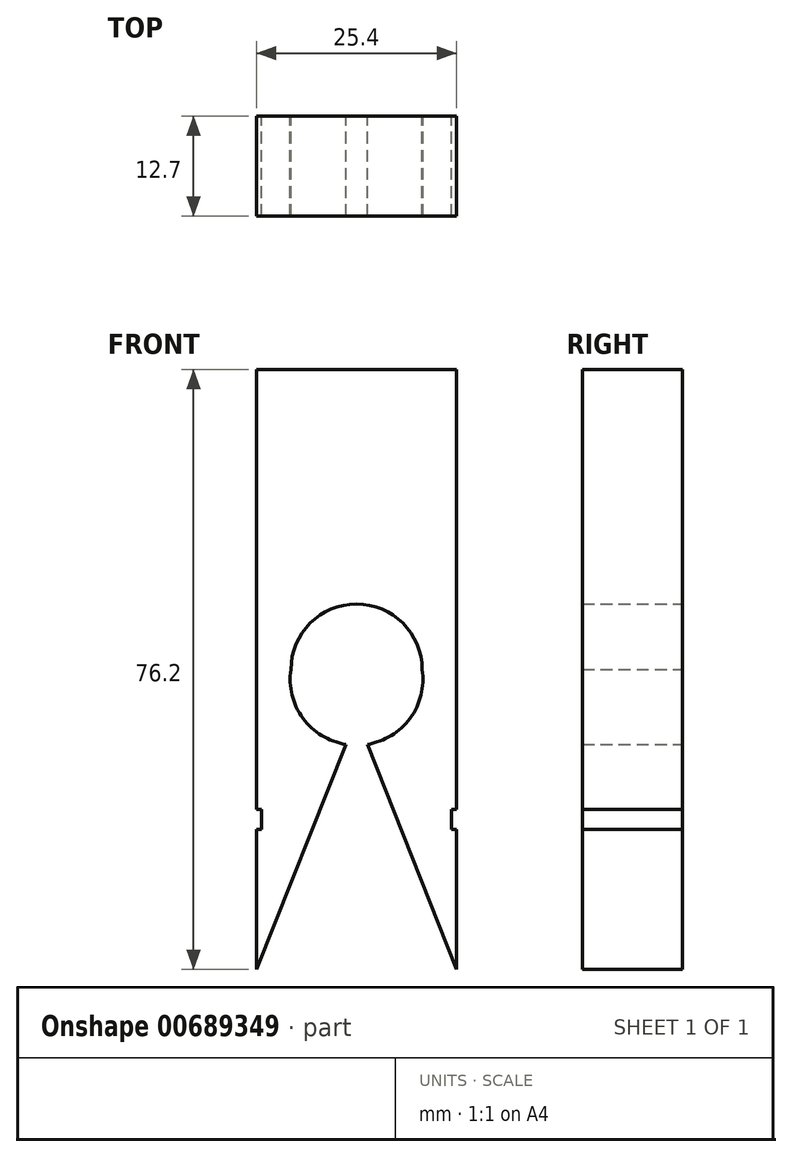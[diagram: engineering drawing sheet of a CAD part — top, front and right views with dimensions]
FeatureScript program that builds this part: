
annotation { "Feature Type Name" : "Feature", "Feature Type Description" : "" }
export const myFeature = defineFeature(function(context is Context, id is Id, definition is map)
    precondition{}
    {
        {
            var Q0;
            Q0=qCreatedBy(makeId("Front.planeOp"),FACE);
            var sketch = newSketch(context, id + "F0", { "sketchPlane" : qUnion([Q0])});
            skArc(sketch, "E0", {"start": v(8.33, 0) * mm, "mid": v(0, 8.33) * mm, "end": v(-8.33, 0) * mm});
            skArc(sketch, "E1", {"start": v(1.37, -9.5) * mm, "mid": v(6.82, -6.2) * mm, "end": v(8.33, 0) * mm});
            skArc(sketch, "E2.MirrorCS", {"start": v(-1.37, -9.5) * mm, "mid": v(-6.82, -6.2) * mm, "end": v(-8.33, 0) * mm});
            skLineSegment(sketch, "E3.bottom", {"start": v(12.7, 38.1) * mm, "end": v(-12.7, 38.1) * mm});
            skLineSegment(sketch, "E3.left", {"start": v(12.7, 38.1) * mm, "end": v(12.7, -17.78) * mm});
            skLineSegment(sketch, "E3.right", {"start": v(-12.7, 38.1) * mm, "end": v(-12.7, -17.78) * mm});
            skLineSegment(sketch, "E4", {"start": v(-1.37, -9.5) * mm, "end": v(-12.7, -38.1) * mm});
            skLineSegment(sketch, "E5", {"start": v(1.37, -9.5) * mm, "end": v(12.7, -38.1) * mm});
            skLineSegment(sketch, "E6", {"start": v(-12.7, -38.1) * mm, "end": v(-12.7, -20.32) * mm});
            skLineSegment(sketch, "E7.bottom", {"start": v(-12.07, -17.78) * mm, "end": v(-12.7, -17.78) * mm});
            skLineSegment(sketch, "E7.top", {"start": v(-12.07, -20.32) * mm, "end": v(-12.7, -20.32) * mm});
            skLineSegment(sketch, "E7.left", {"start": v(-12.07, -17.78) * mm, "end": v(-12.07, -20.32) * mm});
            skPoint(sketch, "E7.middle", {"position": v(-12.7, -19.05) * mm});
            skLineSegment(sketch, "E8.MirrorCS", {"start": v(12.07, -17.78) * mm, "end": v(12.07, -20.32) * mm});
            skLineSegment(sketch, "E9.MirrorCS", {"start": v(12.07, -17.78) * mm, "end": v(12.7, -17.78) * mm});
            skLineSegment(sketch, "E10.MirrorCS", {"start": v(12.07, -20.32) * mm, "end": v(12.7, -20.32) * mm});
            skPoint(sketch, "E11.orphan", {"position": v(-13.34, -17.78) * mm});
            skLineSegment(sketch, "E12.trimOffspring", {"start": v(-12.7, -20.32) * mm, "end": v(-12.7, -38.1) * mm});
            skPoint(sketch, "E13.orphan", {"position": v(-13.34, -20.32) * mm});
            skPoint(sketch, "E14.MirrorCS.end.orphan", {"position": v(13.34, -20.32) * mm});
            skPoint(sketch, "E14.MirrorCS.start.orphan", {"position": v(13.34, -17.78) * mm});
            skLineSegment(sketch, "E15.trimOffspring", {"start": v(12.7, -20.32) * mm, "end": v(12.7, -38.1) * mm});
            skSolve(sketch);
        }
        {
            var Q0;
            Q0 = qSketchRegion(id + "F0", true);
            extrude(context, id + "F1", {"entities" : qUnion([Q0]), "depth" : 12.7 * mm, "offsetDistance" : 25.4 * mm});
        }
    });
